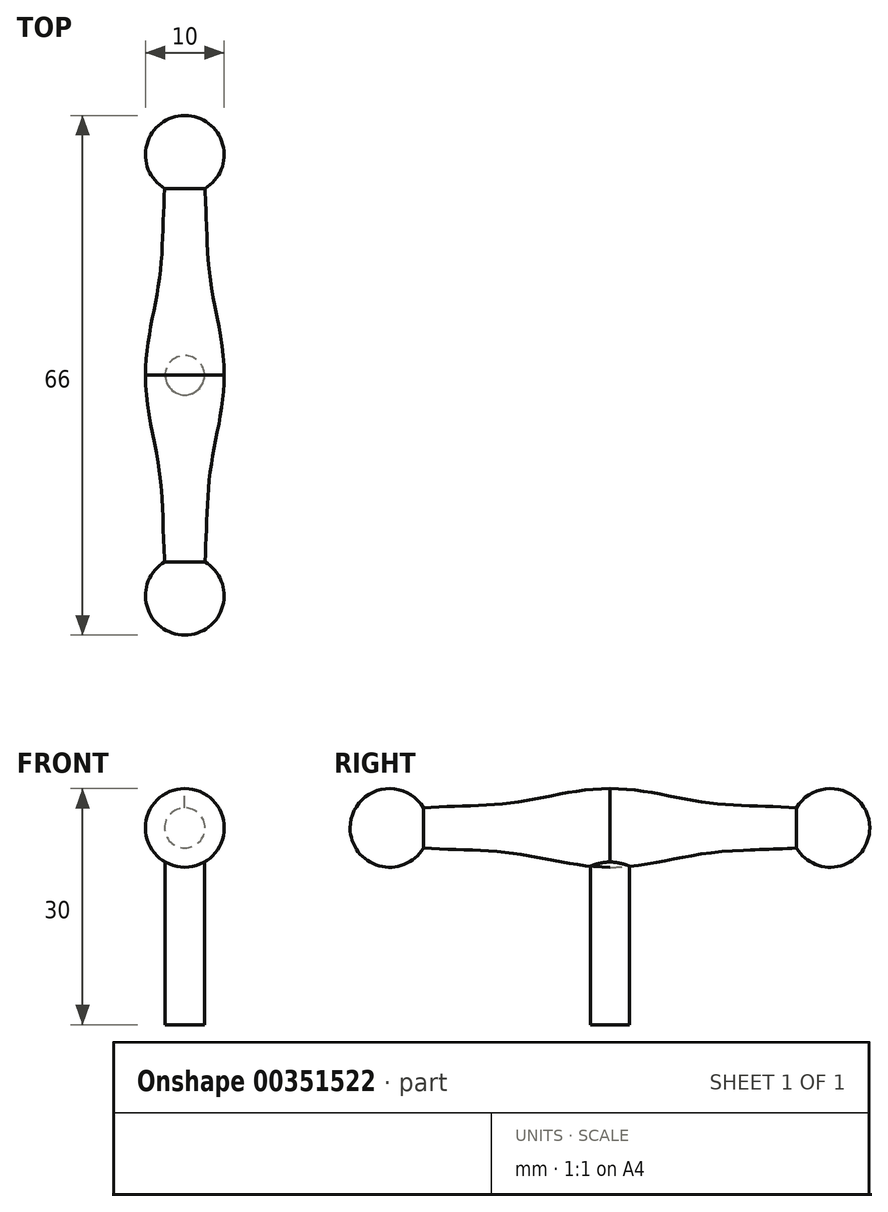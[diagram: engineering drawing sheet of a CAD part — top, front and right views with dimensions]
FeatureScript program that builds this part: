
annotation { "Feature Type Name" : "Feature", "Feature Type Description" : "" }
export const myFeature = defineFeature(function(context is Context, id is Id, definition is map)
    precondition{}
    {
        {
            var Q0;
            Q0=qCreatedBy(makeId("Right.planeOp"),FACE);
            var sketch = newSketch(context, id + "F0", { "sketchPlane" : qUnion([Q0])});
            skLineSegment(sketch, "E0", {"start": v(-32.13, 37.15) * mm, "end": v(-32.13, 22.15) * mm});
            skPoint(sketch, "E1", {"position": v(-32.13, 37.15) * mm});
            skLineSegment(sketch, "E2", {"start": v(-32.13, 37.15) * mm, "end": v(-4.13, 37.15) * mm});
            skLineSegment(sketch, "E3", {"start": v(-32.13, 37.15) * mm, "end": v(-60.13, 37.15) * mm});
            skSolve(sketch);
        }
        {
            var Q0;
            Q0=qCreatedBy(makeId("Right.planeOp"),FACE);
            var sketch = newSketch(context, id + "F1", { "sketchPlane" : qUnion([Q0])});
            skArc(sketch, "E4", {"start": v(-55.13, 37.15) * mm, "mid": v(-60.13, 42.15) * mm, "end": v(-65.13, 37.15) * mm});
            skLineSegment(sketch, "E5", {"start": v(-65.13, 37.15) * mm, "end": v(-55.13, 37.15) * mm});
            skFitSpline(sketch, "E6", {"points": [v(-55.83, 39.7) * mm, v(-44.57, 40.35) * mm, v(-32.13, 42.15) * mm], "startDerivative": vector(22.77, 1.6) * mm, "endDerivative": vector(24.44, -0.04) * mm});
            skLineSegment(sketch, "E7", {"start": v(-32.13, 42.15) * mm, "end": v(-32.13, 37.15) * mm});
            skLineSegment(sketch, "E8", {"start": v(-32.13, 37.15) * mm, "end": v(-55.13, 37.15) * mm});
            skSolve(sketch);
        }
        {
            var Q0;
            {var subQ0=sQuery(id+"F1.wireOp",EDGE,"E5");Q0=makeQuery(id+"F1.imprint","IMPRINT",FACE,{"disambiguationData":[TD([[makeQuery(id+"F1.imprint","IMPRINT",EDGE,{"derivedFrom":subQ0}),1.0]])]});}
            var Q1;
            {var subQ2=sQuery(id+"F1.wireOp",EDGE,"E6");Q1=makeQuery(id+"F1.imprint","IMPRINT",FACE,{"disambiguationData":[TD([[makeQuery(id+"F1.imprint","IMPRINT",EDGE,{"derivedFrom":subQ2}),-1.0]])]});}
            var Q2;
            Q2=sQuery(id+"F1.wireOp",EDGE,"E8");
            revolve(context, id + "F2", {"entities" : qUnion([Q0, Q1]), "axis" : qUnion([Q2]), "revolveType" : RevolveType.FULL});
        }
        {
            var Q0;
            Q0=makeQuery(id+"F2.opRevolve","SWEPT_BODY",BODY,{"disambiguationData":[OSD([sQuery(id+"F1.wireOp",EDGE,"E4"),sQuery(id+"F1.wireOp",EDGE,"E5"),sQuery(id+"F1.wireOp",EDGE,"E6"),sQuery(id+"F1.wireOp",EDGE,"E7"),sQuery(id+"F1.wireOp",EDGE,"E8")])]});
            var Q1;
            Q1=makeQuery(id+"F2.opRevolve","SWEPT_FACE",FACE,{"disambiguationData":[OSD([sQuery(id+"F1.wireOp",EDGE,"E7")])]});
            mirror(context, id + "F3", {"operationType" : NewBodyOperationType.ADD, "entities" : qUnion([Q0]), "mirrorPlane" : qUnion([Q1])});
        }
        {
            var Q0;
            Q0=qCreatedBy(makeId("Top.planeOp"),FACE);
            var Q1;
            Q1=sQuery(id+"F0.wireOp",VERTEX,"E1");
            cPlane(context, id + "F4", {"entities" : qUnion([Q0, Q1]), "cplaneType" : CPlaneType.PLANE_POINT, "offset" : 25 * mm, "width" : 150 * mm, "height" : 150 * mm});
        }
        {
            var Q0;
            Q0=qCreatedBy(id+"F4.planeOp",FACE);
            var sketch = newSketch(context, id + "F5", { "sketchPlane" : qUnion([Q0])});
            skCircle(sketch, "E9", {"center": v(0, -32.13) * mm, "radius": 2.5 * mm});
            skSolve(sketch);
        }
        {
            var Q0;
            Q0 = qSketchRegion(id + "F5", true);
            extrude(context, id + "F6", {"entities" : qUnion([Q0]), "operationType" : NewBodyOperationType.ADD, "oppositeDirection" : true, "depth" : 25 * mm});
        }
    });
